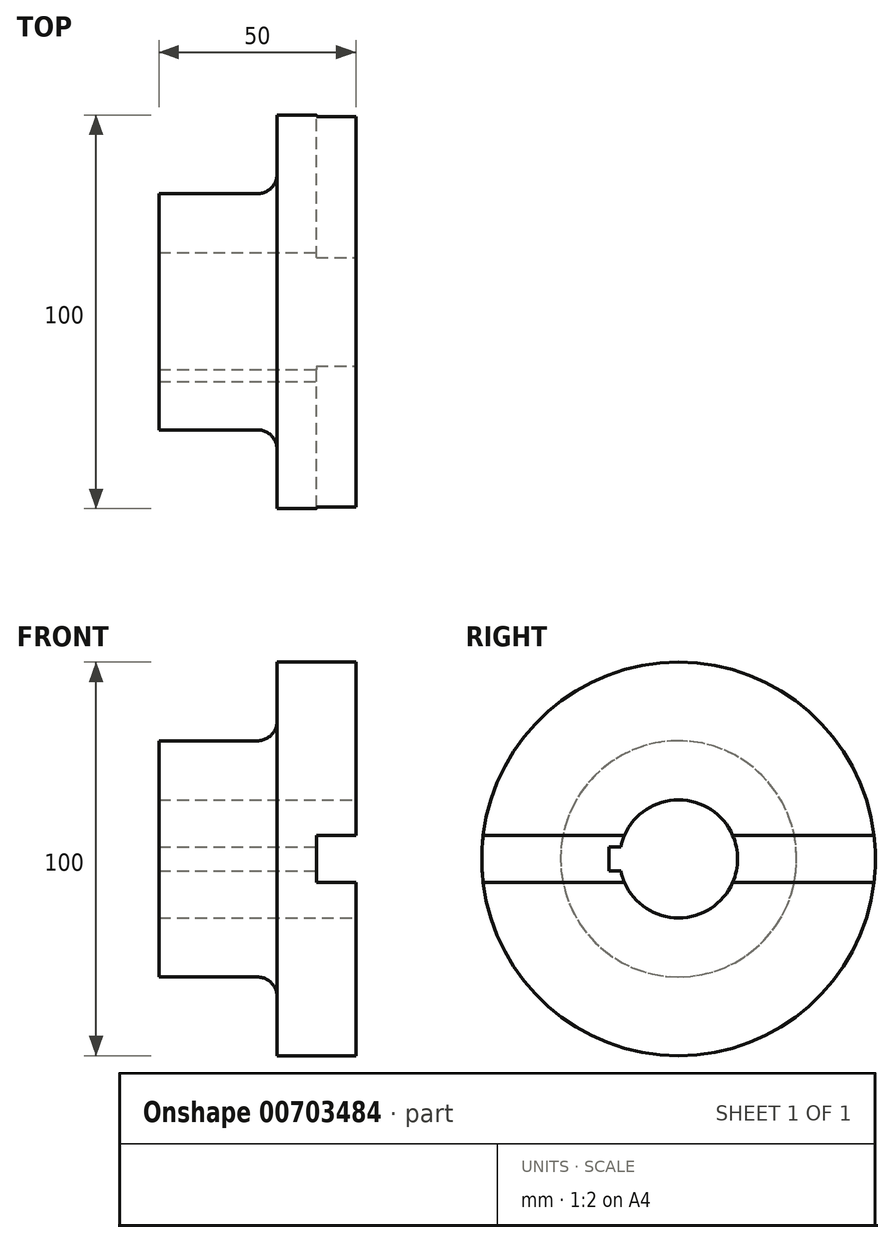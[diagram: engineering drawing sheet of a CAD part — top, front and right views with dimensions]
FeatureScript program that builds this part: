
annotation { "Feature Type Name" : "Feature", "Feature Type Description" : "" }
export const myFeature = defineFeature(function(context is Context, id is Id, definition is map)
    precondition{}
    {
        {
            var Q0;
            Q0=qCreatedBy(makeId("Top.planeOp"),FACE);
            var sketch = newSketch(context, id + "F0", { "sketchPlane" : qUnion([Q0])});
            skLineSegment(sketch, "E0", {"start": v(0, 0) * mm, "end": v(-49.06, 0) * mm});
            skLineSegment(sketch, "E1", {"start": v(0, -15) * mm, "end": v(0, -50) * mm});
            skLineSegment(sketch, "E2", {"start": v(0, -50) * mm, "end": v(-20, -50) * mm});
            skLineSegment(sketch, "E3", {"start": v(-20, -50) * mm, "end": v(-20, -30) * mm});
            skLineSegment(sketch, "E4", {"start": v(-20, -30) * mm, "end": v(-50, -30) * mm});
            skLineSegment(sketch, "E5", {"start": v(-50, -30) * mm, "end": v(-50, -15) * mm});
            skLineSegment(sketch, "E6", {"start": v(-50, -15) * mm, "end": v(0, -15) * mm});
            skLineSegment(sketch, "E7", {"start": v(0, 0) * mm, "end": v(0, -15) * mm, "construction": true});
            skSolve(sketch);
        }
        {
            var Q0;
            Q0=qCreatedBy(makeId("Front.planeOp"),FACE);
            var sketch = newSketch(context, id + "F1", { "sketchPlane" : qUnion([Q0])});
            skLineSegment(sketch, "E8", {"start": v(0, 0) * mm, "end": v(0, 6) * mm});
            skLineSegment(sketch, "E9", {"start": v(0, 6) * mm, "end": v(-10, 6) * mm});
            skLineSegment(sketch, "E10", {"start": v(-10, 6) * mm, "end": v(-10, 0) * mm});
            skLineSegment(sketch, "E11", {"start": v(-10, 0) * mm, "end": v(0, 0) * mm});
            skLineSegment(sketch, "E12.MirrorCS", {"start": v(-10, -6) * mm, "end": v(-10, 0) * mm});
            skLineSegment(sketch, "E13.MirrorCS", {"start": v(0, -6) * mm, "end": v(-10, -6) * mm});
            skLineSegment(sketch, "E14", {"start": v(0, -6) * mm, "end": v(0, 0) * mm});
            skSolve(sketch);
        }
        {
            var Q0;
            Q0=makeQuery(id+"F0.imprint","IMPRINT",FACE,{"disambiguationData":[TD([[makeQuery(id+"F0.imprint","IMPRINT",EDGE,{"derivedFrom":sQuery(id+"F0.wireOp",EDGE,"E1")}),-1.0]])]});
            var Q1;
            Q1=sQuery(id+"F0.wireOp",EDGE,"E0");
            revolve(context, id + "F2", {"surfaceOperationType" : NewSurfaceOperationType.NEW, "entities" : qUnion([Q0]), "axis" : qUnion([Q1]), "revolveType" : RevolveType.FULL});
        }
        {
            var Q0;
            Q0=makeQuery(id+"F1.imprint","IMPRINT",FACE,{"disambiguationData":[TD([[makeQuery(id+"F1.imprint","IMPRINT",EDGE,{"derivedFrom":sQuery(id+"F1.wireOp",EDGE,"E8")}),1.0]])]});
            var Q1;
            Q1=makeQuery(id+"F1.imprint","IMPRINT",FACE,{"disambiguationData":[TD([[makeQuery(id+"F1.imprint","IMPRINT",EDGE,{"derivedFrom":sQuery(id+"F1.wireOp",EDGE,"E11")}),-1.0]])]});
            extrude(context, id + "F3", {"entities" : qUnion([Q0, Q1]), "operationType" : NewBodyOperationType.REMOVE, "depth" : 100 * mm, "offsetDistance" : 25 * mm, "hasSecondDirection" : true, "secondDirectionOppositeDirection" : true, "secondDirectionDepth" : 100 * mm});
        }
        {
            var Q0;
            Q0=qCreatedBy(makeId("Right.planeOp"),FACE);
            var sketch = newSketch(context, id + "F4", { "sketchPlane" : qUnion([Q0])});
            skCircle(sketch, "E15", {"center": v(0, 0) * mm, "radius": 15 * mm});
            skLineSegment(sketch, "E16", {"start": v(0, -15) * mm, "end": v(0, 15) * mm});
            skLineSegment(sketch, "E17", {"start": v(0, -15) * mm, "end": v(0, -17.7) * mm});
            skLineSegment(sketch, "E18", {"start": v(0, -17.7) * mm, "end": v(-3, -17.7) * mm});
            skLineSegment(sketch, "E19", {"start": v(-3, -17.7) * mm, "end": v(-3, -14.7) * mm});
            skLineSegment(sketch, "E20.MirrorCS", {"start": v(3, -17.7) * mm, "end": v(3, -14.7) * mm});
            skLineSegment(sketch, "E21.MirrorCS", {"start": v(0, -17.7) * mm, "end": v(3, -17.7) * mm});
            skLineSegment(sketch, "E22", {"start": v(-3, -14.7) * mm, "end": v(3, -14.7) * mm});
            skLineSegment(sketch, "E23.1.0", {"start": v(17.7, 3) * mm, "end": v(14.7, 3) * mm});
            skLineSegment(sketch, "E23.1.1", {"start": v(14.7, -3) * mm, "end": v(14.7, 3) * mm});
            skLineSegment(sketch, "E23.1.2", {"start": v(17.7, 0) * mm, "end": v(17.7, 3) * mm});
            skLineSegment(sketch, "E23.1.3", {"start": v(17.7, 0) * mm, "end": v(17.7, -3) * mm});
            skLineSegment(sketch, "E23.1.4", {"start": v(17.7, -3) * mm, "end": v(14.7, -3) * mm});
            skLineSegment(sketch, "E23.1.5", {"start": v(15, 0) * mm, "end": v(17.7, 0) * mm});
            skLineSegment(sketch, "E23.2.0", {"start": v(-3, 17.7) * mm, "end": v(-3, 14.7) * mm});
            skLineSegment(sketch, "E23.2.1", {"start": v(3, 14.7) * mm, "end": v(-3, 14.7) * mm});
            skLineSegment(sketch, "E23.2.2", {"start": v(0, 17.7) * mm, "end": v(-3, 17.7) * mm});
            skLineSegment(sketch, "E23.2.3", {"start": v(0, 17.7) * mm, "end": v(3, 17.7) * mm});
            skLineSegment(sketch, "E23.2.4", {"start": v(3, 17.7) * mm, "end": v(3, 14.7) * mm});
            skLineSegment(sketch, "E23.2.5", {"start": v(0, 15) * mm, "end": v(0, 17.7) * mm});
            skLineSegment(sketch, "E23.3.0", {"start": v(-17.7, -3) * mm, "end": v(-14.7, -3) * mm});
            skLineSegment(sketch, "E23.3.1", {"start": v(-14.7, 3) * mm, "end": v(-14.7, -3) * mm});
            skLineSegment(sketch, "E23.3.2", {"start": v(-17.7, 0) * mm, "end": v(-17.7, -3) * mm});
            skLineSegment(sketch, "E23.3.3", {"start": v(-17.7, 0) * mm, "end": v(-17.7, 3) * mm});
            skLineSegment(sketch, "E23.3.4", {"start": v(-17.7, 3) * mm, "end": v(-14.7, 3) * mm});
            skLineSegment(sketch, "E23.3.5", {"start": v(-15, 0) * mm, "end": v(-17.7, 0) * mm});
            skSolve(sketch);
        }
        {
            var Q0;
            Q0=makeQuery(id+"F4.imprint","IMPRINT",FACE,{"disambiguationData":[TD([[makeQuery(id+"F4.imprint","IMPRINT",EDGE,{"derivedFrom":sQuery(id+"F4.wireOp",EDGE,"E23.3.3")}),-1.0]])]});
            var Q1;
            {var subQ0=sQuery(id+"F4.wireOp",EDGE,"E23.3.0");Q1=makeQuery(id+"F4.imprint","IMPRINT",FACE,{"disambiguationData":[TD([[makeQuery(id+"F4.imprint","IMPRINT",EDGE,{"derivedFrom":subQ0}),1.0]])]});}
            extrude(context, id + "F5", {"entities" : qUnion([Q0, Q1]), "operationType" : NewBodyOperationType.REMOVE, "oppositeDirection" : true, "depth" : 100 * mm, "offsetDistance" : 25 * mm});
        }
        {
            var Q0;
            Q0=makeQuery(id+"F2.opRevolve","SWEPT_EDGE",EDGE,{"disambiguationData":[OSD([sQuery(id+"F0.wireOp",EDGE,"E3"),sQuery(id+"F0.wireOp",EDGE,"E4")])]});
            fillet(context, id + "F6", {"entities" : qUnion([Q0]), "radius" : 5 * mm, "tangentPropagation" : true, "allowEdgeOverflow" : false});
        }
    });
